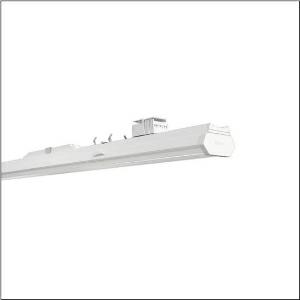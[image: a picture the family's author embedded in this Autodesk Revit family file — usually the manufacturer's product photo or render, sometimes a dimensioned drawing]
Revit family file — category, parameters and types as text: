
# Revit family: licross_r__11_protected_mo_51tp11dn695g_68fa
name_source: partatom
category: Lighting Fixtures
units: mm (PartAtom-declared; Revit-internal decimal feet)

## family parameters
Cut with Voids When Loaded = No
Host = Face
Light Source = No
Part Type = Normal
Room Calculation Point = No
Round Connector Dimension = Use Diameter
Shared = No

## types (1)
- --- (1 x LED, 9680 lm, 57.1 W, 6500K)
    Apparent Load = 57 VA
    CIE Flux Codes = 83 94 98 100 100
    Color Rendering = 80
    Color Temperature = 6500K
    Default Elevation = 1800 mm
    Description = Licross® 11 Protected MO, luminaire insert, of sheet steel, galvanised, coil coated, white, length: 1.500mm, width: 90mm, height: 101mm, LED rated luminous flux: 9.680lm, light colour: 865, control gear: DALI 2, with plug, 5-pole, with phase selection, mains connection: 220..240V, AC, 50/60Hz, rated input power: 57W, internal wiring halogen-free, primary light control with lens, of plastic, primary optical cover: cover, of PMMA, light emission: direct distribution, primary light characteristic: symmetric, protection rating (complete): IP64, insulation class (complete): insulation class I (protective earthing), certification: CE, ENEC, VDE, UKCA, protection symbol: D if used in an environment with conductive dust loads with corresponding accessories, impact resistance: IK06, permissible ambient temperature for indoor applications: -25..+35°C, corresponds to IFS (International Featured Standards) requirements for safety and quality in the food industry, reducing of maximum allowable ambient temperature of 5°C with ceiling mounting, LABS conformity tested according to VDMA 24364:2018-05, packaging unit: 1 piece
    Height = 92 mm
    Lamp = 1 x LED
    Lamp Light Flux = 9680 lm
    Lamp Power = 57.1 W
    Lamp count = 1
    Length = 1500 mm
    Luminous efficacy = 170 lm/W
    Manufacturer = Siteco
    ModVariant = No
    Model = 51TP11DN695G
    Mounting Place = Ceiling
    Mounting Type = Pendant
    Number of Poles = 1
    OnlyDefault = Yes
    Power Factor = 1
    Product Name = Licross® 11 Protected MO
    Product group = luminaire insert | ceiling pendant
    ProductGroupID = 902
    Protection Class = Protection class I
    Protection Degree = IP 64
    RLX_Detail_Level = 1
    RLX_Emergency_Light_Flux = 0 lm
    RLX_Emergency_Type = 0
    RLX_Emergency_Type_DB = No
    RlxData = <blob elided: 24133 chars, md5=df01fe55>
    Socket = socket
    Standby Power = 0 W
    System Light Flux = 9680 lm
    System Power = 57 W
    Type Comments = factory setting: luminous flux: 100 % | dim-lin: 254 | 378 mA
    Type Image = l_1256148.jpg
    URL = http://relux.com
    VarID = @adj_069679
    Voltage = 0 V
    Weight = 0.00 kg
    Width = 88 mm

## geometry (parser evidence)
native form markers: Blend x4, Sweep x12
no freeform markers — native parametric forms only
